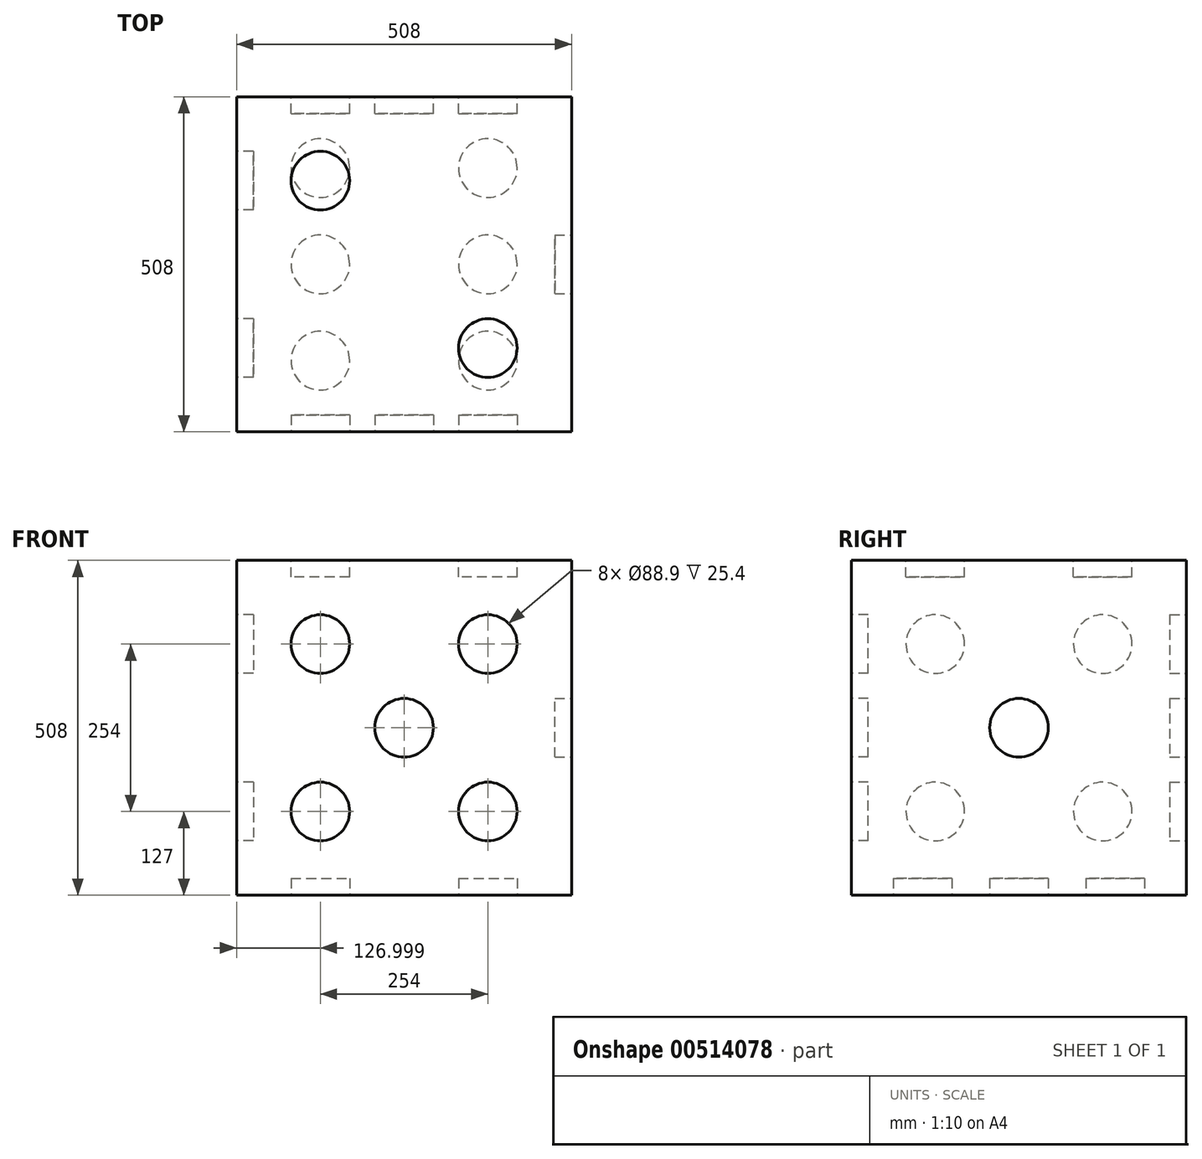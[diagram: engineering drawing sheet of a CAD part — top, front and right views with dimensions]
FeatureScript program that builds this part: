
annotation { "Feature Type Name" : "Feature", "Feature Type Description" : "" }
export const myFeature = defineFeature(function(context is Context, id is Id, definition is map)
    precondition{}
    {
        {
            var Q0;
            Q0=qCreatedBy(makeId("Top.planeOp"),FACE);
            var sketch = newSketch(context, id + "F0", { "sketchPlane" : qUnion([Q0])});
            skLineSegment(sketch, "E0.bottom", {"start": v(-207.08, 298.89) * mm, "end": v(300.92, 298.89) * mm});
            skLineSegment(sketch, "E0.top", {"start": v(-207.08, -209.11) * mm, "end": v(300.92, -209.11) * mm});
            skLineSegment(sketch, "E0.left", {"start": v(-207.08, 298.89) * mm, "end": v(-207.08, -209.11) * mm});
            skLineSegment(sketch, "E0.right", {"start": v(300.92, 298.89) * mm, "end": v(300.92, -209.11) * mm});
            skSolve(sketch);
        }
        {
            var Q0;
            Q0 = qSketchRegion(id + "F0", true);
            extrude(context, id + "F1", {"entities" : qUnion([Q0]), "depth" : 508 * mm});
        }
        {
            var Q0;
            Q0=makeQuery(id+"F1.opExtrude","SWEPT_FACE",FACE,{"disambiguationData":[OSD([sQuery(id+"F0.wireOp",EDGE,"E0.left")])]});
            var sketch = newSketch(context, id + "F2", { "sketchPlane" : qUnion([Q0])});
            skLineSegment(sketch, "E1", {"start": v(-44.89, 508) * mm, "end": v(-44.89, 0) * mm, "construction": true});
            skLineSegment(sketch, "E2", {"start": v(209.11, 254) * mm, "end": v(-298.89, 254) * mm, "construction": true});
            skCircle(sketch, "E3", {"center": v(-171.89, 381) * mm, "radius": 44.45 * mm});
            skCircle(sketch, "E4", {"center": v(82.11, 381) * mm, "radius": 44.45 * mm});
            skCircle(sketch, "E5", {"center": v(-171.89, 127) * mm, "radius": 44.45 * mm});
            skCircle(sketch, "E6", {"center": v(82.11, 127) * mm, "radius": 44.45 * mm});
            skSolve(sketch);
        }
        {
            var Q0;
            Q0=makeQuery(id+"F2.imprint","IMPRINT",FACE,{"disambiguationData":[TD([[makeQuery(id+"F2.imprint","IMPRINT",EDGE,{"derivedFrom":sQuery(id+"F2.wireOp",EDGE,"E5")}),1.0]])]});
            var Q1;
            Q1=makeQuery(id+"F2.imprint","IMPRINT",FACE,{"disambiguationData":[TD([[makeQuery(id+"F2.imprint","IMPRINT",EDGE,{"derivedFrom":sQuery(id+"F2.wireOp",EDGE,"E3")}),1.0]])]});
            var Q2;
            Q2=makeQuery(id+"F2.imprint","IMPRINT",FACE,{"disambiguationData":[TD([[makeQuery(id+"F2.imprint","IMPRINT",EDGE,{"derivedFrom":sQuery(id+"F2.wireOp",EDGE,"E4")}),1.0]])]});
            var Q3;
            Q3=makeQuery(id+"F2.imprint","IMPRINT",FACE,{"disambiguationData":[TD([[makeQuery(id+"F2.imprint","IMPRINT",EDGE,{"derivedFrom":sQuery(id+"F2.wireOp",EDGE,"E6")}),1.0]])]});
            var Q4;
            Q4=sQuery(id+"F2.wireOp",EDGE,"E5");
            var Q5;
            Q5=sQuery(id+"F2.wireOp",EDGE,"E3");
            var Q6;
            Q6=sQuery(id+"F2.wireOp",EDGE,"E4");
            var Q7;
            Q7=sQuery(id+"F2.wireOp",EDGE,"E6");
            extrude(context, id + "F3", {"entities" : qUnion([Q0, Q1, Q2, Q3]), "operationType" : NewBodyOperationType.REMOVE, "surfaceEntities" : qUnion([Q4, Q5, Q6, Q7]), "oppositeDirection" : true, "depth" : 25.4 * mm});
        }
        {
            var Q0;
            Q0=makeQuery(id+"F1.opExtrude","CAP_FACE",FACE,{"disambiguationData":[OSD([sQuery(id+"F0.wireOp",EDGE,"E0.bottom"),sQuery(id+"F0.wireOp",EDGE,"E0.top"),sQuery(id+"F0.wireOp",EDGE,"E0.left"),sQuery(id+"F0.wireOp",EDGE,"E0.right")])],"isStart":true});
            var sketch = newSketch(context, id + "F4", { "sketchPlane" : qUnion([Q0])});
            skLineSegment(sketch, "E7", {"start": v(46.92, 209.11) * mm, "end": v(46.92, -298.89) * mm, "construction": true});
            skLineSegment(sketch, "E8", {"start": v(-207.08, -44.89) * mm, "end": v(300.92, -44.89) * mm, "construction": true});
            skCircle(sketch, "E9", {"center": v(-80.08, 101.16) * mm, "radius": 44.45 * mm});
            skCircle(sketch, "E10", {"center": v(-80.08, -44.89) * mm, "radius": 44.45 * mm});
            skCircle(sketch, "E11", {"center": v(-80.08, -190.94) * mm, "radius": 44.45 * mm});
            skCircle(sketch, "E12", {"center": v(173.92, 101.16) * mm, "radius": 44.45 * mm});
            skCircle(sketch, "E13", {"center": v(173.92, -44.89) * mm, "radius": 44.45 * mm});
            skCircle(sketch, "E14", {"center": v(173.92, -190.94) * mm, "radius": 44.45 * mm});
            skSolve(sketch);
        }
        {
            var Q0;
            Q0=makeQuery(id+"F4.imprint","IMPRINT",FACE,{"disambiguationData":[TD([[makeQuery(id+"F4.imprint","IMPRINT",EDGE,{"derivedFrom":sQuery(id+"F4.wireOp",EDGE,"E9")}),1.0]])]});
            var Q1;
            Q1=makeQuery(id+"F4.imprint","IMPRINT",FACE,{"disambiguationData":[TD([[makeQuery(id+"F4.imprint","IMPRINT",EDGE,{"derivedFrom":sQuery(id+"F4.wireOp",EDGE,"E11")}),1.0]])]});
            var Q2;
            Q2=makeQuery(id+"F4.imprint","IMPRINT",FACE,{"disambiguationData":[TD([[makeQuery(id+"F4.imprint","IMPRINT",EDGE,{"derivedFrom":sQuery(id+"F4.wireOp",EDGE,"E12")}),1.0]])]});
            var Q3;
            Q3=makeQuery(id+"F4.imprint","IMPRINT",FACE,{"disambiguationData":[TD([[makeQuery(id+"F4.imprint","IMPRINT",EDGE,{"derivedFrom":sQuery(id+"F4.wireOp",EDGE,"E10")}),1.0]])]});
            var Q4;
            Q4=makeQuery(id+"F4.imprint","IMPRINT",FACE,{"disambiguationData":[TD([[makeQuery(id+"F4.imprint","IMPRINT",EDGE,{"derivedFrom":sQuery(id+"F4.wireOp",EDGE,"E13")}),1.0]])]});
            var Q5;
            Q5=makeQuery(id+"F4.imprint","IMPRINT",FACE,{"disambiguationData":[TD([[makeQuery(id+"F4.imprint","IMPRINT",EDGE,{"derivedFrom":sQuery(id+"F4.wireOp",EDGE,"E14")}),1.0]])]});
            extrude(context, id + "F5", {"entities" : qUnion([Q0, Q1, Q2, Q3, Q4, Q5]), "operationType" : NewBodyOperationType.REMOVE, "oppositeDirection" : true, "depth" : 25.4 * mm});
        }
        {
            var Q0;
            Q0=makeQuery(id+"F1.opExtrude","SWEPT_FACE",FACE,{"disambiguationData":[OSD([sQuery(id+"F0.wireOp",EDGE,"E0.bottom")])]});
            var sketch = newSketch(context, id + "F6", { "sketchPlane" : qUnion([Q0])});
            skLineSegment(sketch, "E15", {"start": v(-46.92, 0) * mm, "end": v(-46.92, 508) * mm, "construction": true});
            skLineSegment(sketch, "E16", {"start": v(207.08, 254) * mm, "end": v(-300.92, 254) * mm, "construction": true});
            skCircle(sketch, "E17", {"center": v(80.08, 127) * mm, "radius": 44.45 * mm});
            skCircle(sketch, "E18", {"center": v(-46.92, 254) * mm, "radius": 44.45 * mm});
            skCircle(sketch, "E19", {"center": v(-173.92, 381) * mm, "radius": 44.45 * mm});
            skSolve(sketch);
        }
        {
            var Q0;
            Q0=makeQuery(id+"F6.imprint","IMPRINT",FACE,{"disambiguationData":[TD([[makeQuery(id+"F6.imprint","IMPRINT",EDGE,{"derivedFrom":sQuery(id+"F6.wireOp",EDGE,"E17")}),1.0]])]});
            var Q1;
            Q1=makeQuery(id+"F6.imprint","IMPRINT",FACE,{"disambiguationData":[TD([[makeQuery(id+"F6.imprint","IMPRINT",EDGE,{"derivedFrom":sQuery(id+"F6.wireOp",EDGE,"E19")}),1.0]])]});
            var Q2;
            Q2=makeQuery(id+"F6.imprint","IMPRINT",FACE,{"disambiguationData":[TD([[makeQuery(id+"F6.imprint","IMPRINT",EDGE,{"derivedFrom":sQuery(id+"F6.wireOp",EDGE,"E18")}),1.0]])]});
            extrude(context, id + "F7", {"entities" : qUnion([Q0, Q1, Q2]), "operationType" : NewBodyOperationType.REMOVE, "oppositeDirection" : true, "depth" : 25.4 * mm});
        }
        {
            var Q0;
            Q0=makeQuery(id+"F1.opExtrude","SWEPT_FACE",FACE,{"disambiguationData":[OSD([sQuery(id+"F0.wireOp",EDGE,"E0.top")])]});
            var sketch = newSketch(context, id + "F8", { "sketchPlane" : qUnion([Q0])});
            skCircle(sketch, "E20", {"center": v(-80.08, 381) * mm, "radius": 44.45 * mm});
            skCircle(sketch, "E21", {"center": v(173.92, 381) * mm, "radius": 44.45 * mm});
            skCircle(sketch, "E22", {"center": v(-80.08, 127) * mm, "radius": 44.45 * mm});
            skCircle(sketch, "E23", {"center": v(173.92, 127) * mm, "radius": 44.45 * mm});
            skCircle(sketch, "E24", {"center": v(46.92, 254) * mm, "radius": 44.45 * mm});
            skPoint(sketch, "E24.centerSnap0", {"position": v(-207.08, 254) * mm});
            skPoint(sketch, "E24.centerSnap1", {"position": v(46.92, 0) * mm});
            skSolve(sketch);
        }
        {
            var Q0;
            Q0=makeQuery(id+"F8.imprint","IMPRINT",FACE,{"disambiguationData":[TD([[makeQuery(id+"F8.imprint","IMPRINT",EDGE,{"derivedFrom":sQuery(id+"F8.wireOp",EDGE,"E22")}),1.0]])]});
            var Q1;
            Q1=makeQuery(id+"F8.imprint","IMPRINT",FACE,{"disambiguationData":[TD([[makeQuery(id+"F8.imprint","IMPRINT",EDGE,{"derivedFrom":sQuery(id+"F8.wireOp",EDGE,"E20")}),1.0]])]});
            var Q2;
            Q2=makeQuery(id+"F8.imprint","IMPRINT",FACE,{"disambiguationData":[TD([[makeQuery(id+"F8.imprint","IMPRINT",EDGE,{"derivedFrom":sQuery(id+"F8.wireOp",EDGE,"E24")}),1.0]])]});
            var Q3;
            Q3=makeQuery(id+"F8.imprint","IMPRINT",FACE,{"disambiguationData":[TD([[makeQuery(id+"F8.imprint","IMPRINT",EDGE,{"derivedFrom":sQuery(id+"F8.wireOp",EDGE,"E23")}),1.0]])]});
            var Q4;
            Q4=makeQuery(id+"F8.imprint","IMPRINT",FACE,{"disambiguationData":[TD([[makeQuery(id+"F8.imprint","IMPRINT",EDGE,{"derivedFrom":sQuery(id+"F8.wireOp",EDGE,"E21")}),1.0]])]});
            extrude(context, id + "F9", {"entities" : qUnion([Q0, Q1, Q2, Q3, Q4]), "operationType" : NewBodyOperationType.REMOVE, "oppositeDirection" : true, "depth" : 25.4 * mm});
        }
        {
            var Q0;
            Q0=makeQuery(id+"F1.opExtrude","SWEPT_FACE",FACE,{"disambiguationData":[OSD([sQuery(id+"F0.wireOp",EDGE,"E0.right")])]});
            var sketch = newSketch(context, id + "F10", { "sketchPlane" : qUnion([Q0])});
            skCircle(sketch, "E25", {"center": v(44.89, 254) * mm, "radius": 44.45 * mm});
            skPoint(sketch, "E25.centerSnap0", {"position": v(44.89, 508) * mm});
            skPoint(sketch, "E25.centerSnap1", {"position": v(298.89, 254) * mm});
            skSolve(sketch);
        }
        {
            var Q0;
            Q0=makeQuery(id+"F10.imprint","IMPRINT",FACE,{"disambiguationData":[TD([[makeQuery(id+"F10.imprint","IMPRINT",EDGE,{"derivedFrom":sQuery(id+"F10.wireOp",EDGE,"E25")}),1.0]])]});
            var Q1;
            Q1=sQuery(id+"F10.wireOp",EDGE,"E25");
            extrude(context, id + "F11", {"entities" : qUnion([Q0]), "operationType" : NewBodyOperationType.REMOVE, "surfaceEntities" : qUnion([Q1]), "oppositeDirection" : true, "depth" : 25.4 * mm});
        }
        {
            var Q0;
            Q0=makeQuery(id+"F1.opExtrude","CAP_FACE",FACE,{"disambiguationData":[OSD([sQuery(id+"F0.wireOp",EDGE,"E0.bottom"),sQuery(id+"F0.wireOp",EDGE,"E0.top"),sQuery(id+"F0.wireOp",EDGE,"E0.left"),sQuery(id+"F0.wireOp",EDGE,"E0.right")])],"isStart":false});
            var sketch = newSketch(context, id + "F12", { "sketchPlane" : qUnion([Q0])});
            skLineSegment(sketch, "E26", {"start": v(46.92, 298.89) * mm, "end": v(46.92, -209.11) * mm, "construction": true});
            skLineSegment(sketch, "E27", {"start": v(300.92, 44.89) * mm, "end": v(-207.08, 44.89) * mm, "construction": true});
            skCircle(sketch, "E28", {"center": v(-80.08, 171.89) * mm, "radius": 44.45 * mm});
            skCircle(sketch, "E29", {"center": v(173.92, -82.11) * mm, "radius": 44.45 * mm});
            skSolve(sketch);
        }
        {
            var Q0;
            Q0=makeQuery(id+"F12.imprint","IMPRINT",FACE,{"disambiguationData":[TD([[makeQuery(id+"F12.imprint","IMPRINT",EDGE,{"derivedFrom":sQuery(id+"F12.wireOp",EDGE,"E29")}),1.0]])]});
            var Q1;
            Q1=makeQuery(id+"F12.imprint","IMPRINT",FACE,{"disambiguationData":[TD([[makeQuery(id+"F12.imprint","IMPRINT",EDGE,{"derivedFrom":sQuery(id+"F12.wireOp",EDGE,"E28")}),1.0]])]});
            var Q2;
            Q2=sQuery(id+"F12.wireOp",EDGE,"E28");
            extrude(context, id + "F13", {"entities" : qUnion([Q0, Q1]), "operationType" : NewBodyOperationType.REMOVE, "surfaceEntities" : qUnion([Q2]), "oppositeDirection" : true, "depth" : 25.4 * mm});
        }
    });
